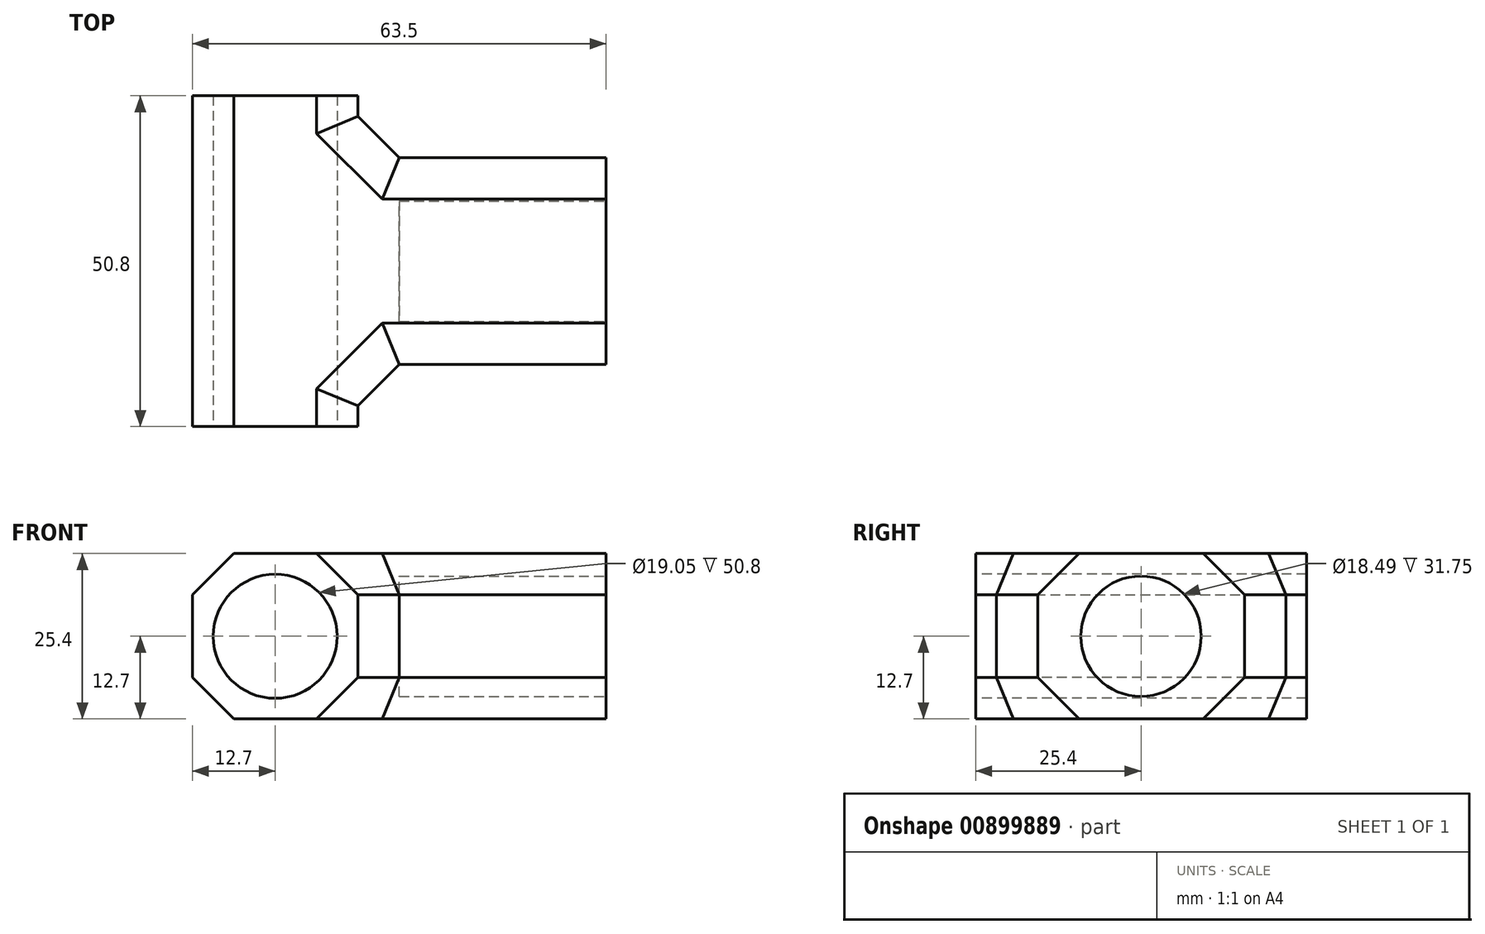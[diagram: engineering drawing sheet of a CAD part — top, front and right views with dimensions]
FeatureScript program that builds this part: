
annotation { "Feature Type Name" : "Feature", "Feature Type Description" : "" }
export const myFeature = defineFeature(function(context is Context, id is Id, definition is map)
    precondition{}
    {
        {
            var Q0;
            Q0=qCreatedBy(makeId("Top.planeOp"),FACE);
            var sketch = newSketch(context, id + "F0", { "sketchPlane" : qUnion([Q0])});
            skLineSegment(sketch, "E0.bottom", {"start": v(-12.7, 15.88) * mm, "end": v(25.4, 15.88) * mm});
            skLineSegment(sketch, "E0.top", {"start": v(-12.7, -15.88) * mm, "end": v(25.4, -15.88) * mm});
            skLineSegment(sketch, "E0.right", {"start": v(25.4, 15.88) * mm, "end": v(25.4, -15.88) * mm});
            skPoint(sketch, "E0.middle", {"position": v(0, 0) * mm});
            skLineSegment(sketch, "E1.bottom", {"start": v(-12.7, 25.4) * mm, "end": v(-38.1, 25.4) * mm});
            skLineSegment(sketch, "E1.top", {"start": v(-12.7, -25.4) * mm, "end": v(-38.1, -25.4) * mm});
            skLineSegment(sketch, "E1.left", {"start": v(-12.7, 25.4) * mm, "end": v(-12.7, 15.88) * mm});
            skLineSegment(sketch, "E1.right", {"start": v(-38.1, 25.4) * mm, "end": v(-38.1, -25.4) * mm});
            skPoint(sketch, "E1.middle", {"position": v(-25.4, 0) * mm});
            skPoint(sketch, "E2.orphan", {"position": v(-25.4, 15.88) * mm});
            skPoint(sketch, "E0.left.end.orphan", {"position": v(-25.4, -15.88) * mm});
            skLineSegment(sketch, "E3.trimOffspring", {"start": v(-12.7, -15.88) * mm, "end": v(-12.7, -25.4) * mm});
            skSolve(sketch);
        }
        {
            var Q0;
            Q0 = qSketchRegion(id + "F0", true);
            extrude(context, id + "F1", {"entities" : qUnion([Q0]), "depth" : 25.4 * mm, "offsetDistance" : 25.4 * mm});
        }
        {
            var Q0;
            Q0=makeQuery(id+"F1.opExtrude","SWEPT_FACE",FACE,{"disambiguationData":[OSD([sQuery(id+"F0.wireOp",EDGE,"E1.top")])]});
            var sketch = newSketch(context, id + "F2", { "sketchPlane" : qUnion([Q0])});
            skLineSegment(sketch, "E4", {"start": v(-25.4, 25.4) * mm, "end": v(-25.4, 0) * mm, "construction": true});
            skLineSegment(sketch, "E5", {"start": v(-25.4, 0) * mm, "end": v(-12.7, 12.7) * mm, "construction": true});
            skLineSegment(sketch, "E6", {"start": v(-12.7, 12.7) * mm, "end": v(-38.1, 12.7) * mm, "construction": true});
            skCircle(sketch, "E7", {"center": v(-25.4, 12.7) * mm, "radius": 9.53 * mm});
            skSolve(sketch);
        }
        {
            var Q0;
            Q0 = qSketchRegion(id + "F2", true);
            extrude(context, id + "F3", {"entities" : qUnion([Q0]), "operationType" : NewBodyOperationType.REMOVE, "oppositeDirection" : true, "depth" : 91.19 * mm, "offsetDistance" : 25.4 * mm});
        }
        {
            var Q0;
            Q0=makeQuery(id+"F1.opExtrude","SWEPT_FACE",FACE,{"disambiguationData":[OSD([sQuery(id+"F0.wireOp",EDGE,"E0.right")])]});
            var sketch = newSketch(context, id + "F4", { "sketchPlane" : qUnion([Q0])});
            skLineSegment(sketch, "E8", {"start": v(0, 25.4) * mm, "end": v(0, 0) * mm, "construction": true});
            skCircle(sketch, "E9", {"center": v(0, 12.7) * mm, "radius": 9.24 * mm});
            skSolve(sketch);
        }
        {
            var Q0;
            Q0=makeQuery(id+"F4.imprint","IMPRINT",FACE,{"disambiguationData":[TD([[makeQuery(id+"F4.imprint","IMPRINT",EDGE,{"derivedFrom":sQuery(id+"F4.wireOp",EDGE,"E9")}),1.0]])]});
            extrude(context, id + "F5", {"entities" : qUnion([Q0]), "operationType" : NewBodyOperationType.REMOVE, "oppositeDirection" : true, "depth" : 31.75 * mm, "offsetDistance" : 25.4 * mm});
        }
        {
            var Q0;
            Q0=makeQuery(id+"F1.opExtrude","SWEPT_EDGE",EDGE,{"disambiguationData":[OSD([sQuery(id+"F0.wireOp",EDGE,"E0.bottom"),sQuery(id+"F0.wireOp",EDGE,"E1.left")])]});
            var Q1;
            Q1=makeQuery(id+"F1.opExtrude","SWEPT_EDGE",EDGE,{"disambiguationData":[OSD([sQuery(id+"F0.wireOp",EDGE,"E0.top"),sQuery(id+"F0.wireOp",EDGE,"E3.trimOffspring")])]});
            chamfer(context, id + "F6", {"entities" : qUnion([Q0, Q1]), "width" : 6.35 * mm, "tangentPropagation" : true});
        }
        {
            var Q0;
            Q0=makeQuery(id+"F1.opExtrude","CAP_EDGE",EDGE,{"disambiguationData":[OSD([sQuery(id+"F0.wireOp",EDGE,"E3.trimOffspring")])],"isStart":false});
            var Q1;
            {var subQ0=sQuery(id+"F0.wireOp",EDGE,"E3.trimOffspring");var subQ1=sQuery(id+"F0.wireOp",EDGE,"E0.top");Q1=makeQuery(id+"F6.opChamfer","BLEND_EDGE",EDGE,{"blendedFrom":[makeQuery(id+"F1.opExtrude","SWEPT_EDGE",EDGE,{"disambiguationData":[OSD([subQ1,subQ0])]}),makeQuery(id+"F1.opExtrude","CAP_FACE",FACE,{"disambiguationData":[OSD([sQuery(id+"F0.wireOp",EDGE,"E0.bottom"),subQ1,sQuery(id+"F0.wireOp",EDGE,"E0.right"),sQuery(id+"F0.wireOp",EDGE,"E1.bottom"),sQuery(id+"F0.wireOp",EDGE,"E1.top"),sQuery(id+"F0.wireOp",EDGE,"E1.left"),sQuery(id+"F0.wireOp",EDGE,"E1.right"),subQ0])],"isStart":false})],"blendedInto":[makeQuery(id+"F1.opExtrude","CAP_FACE",FACE,{"disambiguationData":[OSD([sQuery(id+"F0.wireOp",EDGE,"E0.bottom"),subQ1,sQuery(id+"F0.wireOp",EDGE,"E0.right"),sQuery(id+"F0.wireOp",EDGE,"E1.bottom"),sQuery(id+"F0.wireOp",EDGE,"E1.top"),sQuery(id+"F0.wireOp",EDGE,"E1.left"),sQuery(id+"F0.wireOp",EDGE,"E1.right"),subQ0])],"isStart":false})]});}
            var Q2;
            Q2=makeQuery(id+"F1.opExtrude","CAP_EDGE",EDGE,{"disambiguationData":[OSD([sQuery(id+"F0.wireOp",EDGE,"E0.top")])],"isStart":false});
            var Q3;
            Q3=makeQuery(id+"F1.opExtrude","CAP_EDGE",EDGE,{"disambiguationData":[OSD([sQuery(id+"F0.wireOp",EDGE,"E0.bottom")])],"isStart":false});
            var Q4;
            {var subQ0=sQuery(id+"F0.wireOp",EDGE,"E1.left");var subQ1=sQuery(id+"F0.wireOp",EDGE,"E0.bottom");Q4=makeQuery(id+"F6.opChamfer","BLEND_EDGE",EDGE,{"blendedFrom":[makeQuery(id+"F1.opExtrude","SWEPT_EDGE",EDGE,{"disambiguationData":[OSD([subQ1,subQ0])]}),makeQuery(id+"F1.opExtrude","CAP_FACE",FACE,{"disambiguationData":[OSD([subQ1,sQuery(id+"F0.wireOp",EDGE,"E0.top"),sQuery(id+"F0.wireOp",EDGE,"E0.right"),sQuery(id+"F0.wireOp",EDGE,"E1.bottom"),sQuery(id+"F0.wireOp",EDGE,"E1.top"),subQ0,sQuery(id+"F0.wireOp",EDGE,"E1.right"),sQuery(id+"F0.wireOp",EDGE,"E3.trimOffspring")])],"isStart":false})],"blendedInto":[makeQuery(id+"F1.opExtrude","CAP_FACE",FACE,{"disambiguationData":[OSD([subQ1,sQuery(id+"F0.wireOp",EDGE,"E0.top"),sQuery(id+"F0.wireOp",EDGE,"E0.right"),sQuery(id+"F0.wireOp",EDGE,"E1.bottom"),sQuery(id+"F0.wireOp",EDGE,"E1.top"),subQ0,sQuery(id+"F0.wireOp",EDGE,"E1.right"),sQuery(id+"F0.wireOp",EDGE,"E3.trimOffspring")])],"isStart":false})]});}
            var Q5;
            Q5=makeQuery(id+"F1.opExtrude","CAP_EDGE",EDGE,{"disambiguationData":[OSD([sQuery(id+"F0.wireOp",EDGE,"E1.left")])],"isStart":false});
            var Q6;
            Q6=makeQuery(id+"F1.opExtrude","CAP_EDGE",EDGE,{"disambiguationData":[OSD([sQuery(id+"F0.wireOp",EDGE,"E1.right")])],"isStart":false});
            var Q7;
            Q7=makeQuery(id+"F1.opExtrude","CAP_EDGE",EDGE,{"disambiguationData":[OSD([sQuery(id+"F0.wireOp",EDGE,"E0.bottom")])],"isStart":true});
            var Q8;
            {var subQ0=sQuery(id+"F0.wireOp",EDGE,"E1.left");var subQ1=sQuery(id+"F0.wireOp",EDGE,"E0.bottom");Q8=makeQuery(id+"F6.opChamfer","BLEND_EDGE",EDGE,{"blendedFrom":[makeQuery(id+"F1.opExtrude","SWEPT_EDGE",EDGE,{"disambiguationData":[OSD([subQ1,subQ0])]}),makeQuery(id+"F1.opExtrude","CAP_FACE",FACE,{"disambiguationData":[OSD([subQ1,sQuery(id+"F0.wireOp",EDGE,"E0.top"),sQuery(id+"F0.wireOp",EDGE,"E0.right"),sQuery(id+"F0.wireOp",EDGE,"E1.bottom"),sQuery(id+"F0.wireOp",EDGE,"E1.top"),subQ0,sQuery(id+"F0.wireOp",EDGE,"E1.right"),sQuery(id+"F0.wireOp",EDGE,"E3.trimOffspring")])],"isStart":true})],"blendedInto":[makeQuery(id+"F1.opExtrude","CAP_FACE",FACE,{"disambiguationData":[OSD([subQ1,sQuery(id+"F0.wireOp",EDGE,"E0.top"),sQuery(id+"F0.wireOp",EDGE,"E0.right"),sQuery(id+"F0.wireOp",EDGE,"E1.bottom"),sQuery(id+"F0.wireOp",EDGE,"E1.top"),subQ0,sQuery(id+"F0.wireOp",EDGE,"E1.right"),sQuery(id+"F0.wireOp",EDGE,"E3.trimOffspring")])],"isStart":true})]});}
            var Q9;
            Q9=makeQuery(id+"F1.opExtrude","CAP_EDGE",EDGE,{"disambiguationData":[OSD([sQuery(id+"F0.wireOp",EDGE,"E1.left")])],"isStart":true});
            var Q10;
            Q10=makeQuery(id+"F1.opExtrude","CAP_EDGE",EDGE,{"disambiguationData":[OSD([sQuery(id+"F0.wireOp",EDGE,"E1.right")])],"isStart":true});
            var Q11;
            Q11=makeQuery(id+"F1.opExtrude","CAP_EDGE",EDGE,{"disambiguationData":[OSD([sQuery(id+"F0.wireOp",EDGE,"E3.trimOffspring")])],"isStart":true});
            var Q12;
            {var subQ0=sQuery(id+"F0.wireOp",EDGE,"E3.trimOffspring");var subQ1=sQuery(id+"F0.wireOp",EDGE,"E0.top");Q12=makeQuery(id+"F6.opChamfer","BLEND_EDGE",EDGE,{"blendedFrom":[makeQuery(id+"F1.opExtrude","SWEPT_EDGE",EDGE,{"disambiguationData":[OSD([subQ1,subQ0])]}),makeQuery(id+"F1.opExtrude","CAP_FACE",FACE,{"disambiguationData":[OSD([sQuery(id+"F0.wireOp",EDGE,"E0.bottom"),subQ1,sQuery(id+"F0.wireOp",EDGE,"E0.right"),sQuery(id+"F0.wireOp",EDGE,"E1.bottom"),sQuery(id+"F0.wireOp",EDGE,"E1.top"),sQuery(id+"F0.wireOp",EDGE,"E1.left"),sQuery(id+"F0.wireOp",EDGE,"E1.right"),subQ0])],"isStart":true})],"blendedInto":[makeQuery(id+"F1.opExtrude","CAP_FACE",FACE,{"disambiguationData":[OSD([sQuery(id+"F0.wireOp",EDGE,"E0.bottom"),subQ1,sQuery(id+"F0.wireOp",EDGE,"E0.right"),sQuery(id+"F0.wireOp",EDGE,"E1.bottom"),sQuery(id+"F0.wireOp",EDGE,"E1.top"),sQuery(id+"F0.wireOp",EDGE,"E1.left"),sQuery(id+"F0.wireOp",EDGE,"E1.right"),subQ0])],"isStart":true})]});}
            var Q13;
            Q13=makeQuery(id+"F1.opExtrude","CAP_EDGE",EDGE,{"disambiguationData":[OSD([sQuery(id+"F0.wireOp",EDGE,"E0.top")])],"isStart":true});
            chamfer(context, id + "F7", {"entities" : qUnion([Q0, Q1, Q2, Q3, Q4, Q5, Q6, Q7, Q8, Q9, Q10, Q11, Q12, Q13]), "width" : 6.35 * mm, "tangentPropagation" : true});
        }
    });
